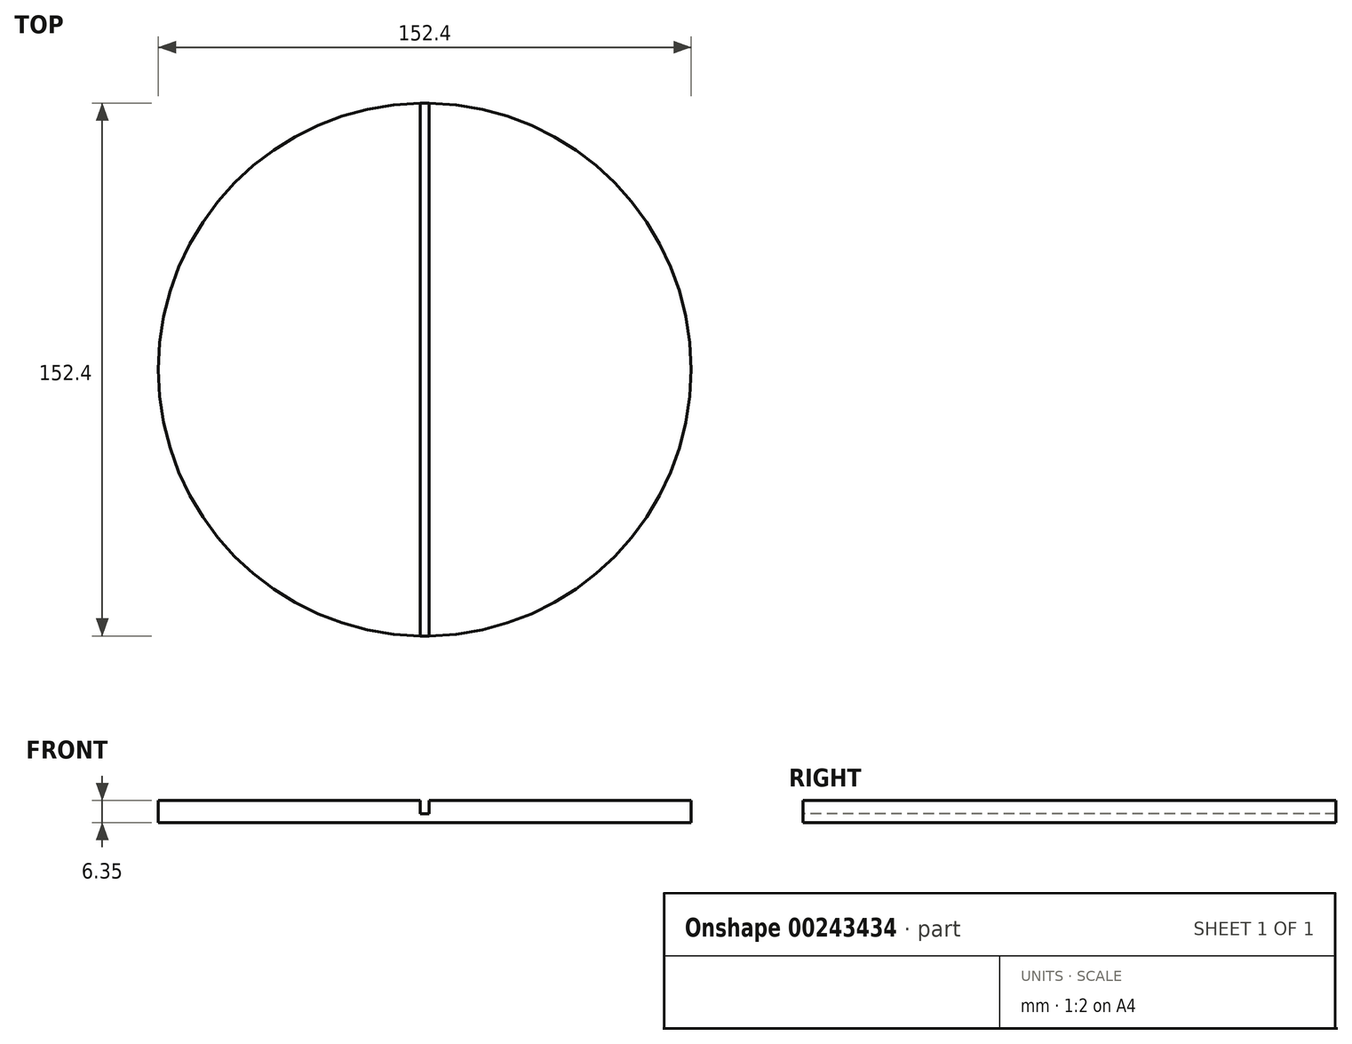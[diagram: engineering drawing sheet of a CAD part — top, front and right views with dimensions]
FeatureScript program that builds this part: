
annotation { "Feature Type Name" : "Feature", "Feature Type Description" : "" }
export const myFeature = defineFeature(function(context is Context, id is Id, definition is map)
    precondition{}
    {
        {
            var Q0;
            Q0=qCreatedBy(makeId("Top.planeOp"),FACE);
            var sketch = newSketch(context, id + "F0", { "sketchPlane" : qUnion([Q0])});
            skCircle(sketch, "E0", {"center": v(0, 0) * mm, "radius": 76.2 * mm});
            skSolve(sketch);
        }
        {
            var Q0;
            Q0=makeQuery(id+"F0.imprint","IMPRINT",FACE,{"disambiguationData":[TD([[makeQuery(id+"F0.imprint","IMPRINT",EDGE,{"derivedFrom":sQuery(id+"F0.wireOp",EDGE,"E0")}),1.0]])]});
            extrude(context, id + "F1", {"entities" : qUnion([Q0]), "depth" : 6.35 * mm});
        }
        {
            var Q0;
            Q0=makeQuery(id+"F1.opExtrude","CAP_FACE",FACE,{"disambiguationData":[OSD([sQuery(id+"F0.wireOp",EDGE,"E0")])],"isStart":false});
            var sketch = newSketch(context, id + "F2", { "sketchPlane" : qUnion([Q0])});
            skLineSegment(sketch, "E1.bottom", {"start": v(-1.27, 76.2) * mm, "end": v(1.27, 76.2) * mm});
            skLineSegment(sketch, "E1.top", {"start": v(-1.27, -76.2) * mm, "end": v(1.27, -76.2) * mm});
            skLineSegment(sketch, "E1.left", {"start": v(-1.27, 76.2) * mm, "end": v(-1.27, -76.2) * mm});
            skLineSegment(sketch, "E1.right", {"start": v(1.27, 76.2) * mm, "end": v(1.27, -76.2) * mm});
            skSolve(sketch);
        }
        {
            var Q0;
            {var subQ0=sQuery(id+"F2.wireOp",EDGE,"E1.left");var subQ1=sQuery(id+"F2.wireOp",EDGE,"E1.bottom");var subQ2=makeQuery(id+"F2.imprint","INTERSECT",VERTEX,{"derivedFrom":[subQ1,subQ0]});Q0=makeQuery(id+"F2.imprint","IMPRINT",FACE,{"disambiguationData":[TD([[makeQuery(id+"F2.imprint","IMPRINT",EDGE,{"disambiguationData":[TD([[subQ2,-1.0]])],"derivedFrom":subQ1}),-1.0]])]});}
            var Q1;
            {var subQ0=sQuery(id+"F2.wireOp",EDGE,"E1.right");var subQ1=sQuery(id+"F2.wireOp",EDGE,"E1.bottom");var subQ2=makeQuery(id+"F2.imprint","INTERSECT",VERTEX,{"derivedFrom":[subQ1,subQ0]});Q1=makeQuery(id+"F2.imprint","IMPRINT",FACE,{"disambiguationData":[TD([[makeQuery(id+"F2.imprint","IMPRINT",EDGE,{"disambiguationData":[TD([[subQ2,1.0]])],"derivedFrom":subQ1}),-1.0]])]});}
            var Q2;
            {var subQ0=sQuery(id+"F2.wireOp",EDGE,"E1.left");var subQ1=sQuery(id+"F2.wireOp",EDGE,"E1.top");var subQ2=makeQuery(id+"F2.imprint","INTERSECT",VERTEX,{"derivedFrom":[subQ1,subQ0]});Q2=makeQuery(id+"F2.imprint","IMPRINT",FACE,{"disambiguationData":[TD([[makeQuery(id+"F2.imprint","IMPRINT",EDGE,{"disambiguationData":[TD([[subQ2,-1.0]])],"derivedFrom":subQ1}),1.0]])]});}
            var Q3;
            {var subQ0=sQuery(id+"F2.wireOp",EDGE,"E1.right");var subQ1=sQuery(id+"F2.wireOp",EDGE,"E1.top");var subQ2=makeQuery(id+"F2.imprint","INTERSECT",VERTEX,{"derivedFrom":[subQ1,subQ0]});Q3=makeQuery(id+"F2.imprint","IMPRINT",FACE,{"disambiguationData":[TD([[makeQuery(id+"F2.imprint","IMPRINT",EDGE,{"disambiguationData":[TD([[subQ2,1.0]])],"derivedFrom":subQ1}),1.0]])]});}
            var Q4;
            {var subQ1=makeQuery(id+"F1.opExtrude","CAP_EDGE",EDGE,{"disambiguationData":[OSD([sQuery(id+"F0.wireOp",EDGE,"E0")])],"isStart":false});var subQ5=sQuery(id+"F2.wireOp",EDGE,"E1.left");var subQ6=makeQuery(id+"F2.imprint","INTERSECT",VERTEX,{"disambiguationData":[OD(0.0)],"derivedFrom":[subQ1,subQ5]});Q4=makeQuery(id+"F2.imprint","IMPRINT",FACE,{"disambiguationData":[TD([[makeQuery(id+"F2.imprint","IMPRINT",EDGE,{"disambiguationData":[TD([[subQ6,-1.0]])],"derivedFrom":subQ5}),1.0]])]});}
            extrude(context, id + "F3", {"entities" : qUnion([Q0, Q1, Q2, Q3, Q4]), "operationType" : NewBodyOperationType.REMOVE, "oppositeDirection" : true, "depth" : 3.8 * mm});
        }
    });
